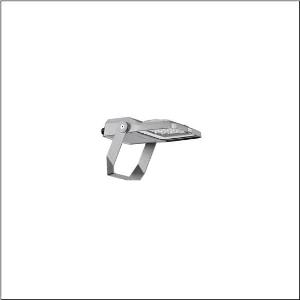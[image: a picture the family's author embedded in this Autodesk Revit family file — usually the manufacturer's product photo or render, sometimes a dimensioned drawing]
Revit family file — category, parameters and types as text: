
# Revit family: floodlight_fl_21_iq_micro___rs12_5xa7762a2b1a_2903
name_source: partatom
category: Lighting Fixtures
units: mm (PartAtom-declared; Revit-internal decimal feet)

## family parameters
Cut with Voids When Loaded = No
Host = Face
Light Source = No
Part Type = Normal
Room Calculation Point = No
Round Connector Dimension = Use Diameter
Shared = No

## types (1)
- --- (1 x LED, 3090 lm, 23.1 W, 3000K)
    Apparent Load = 23 VA
    CIE Flux Codes = 79 92 99 100 100
    Color Rendering = 70
    Color Temperature = 3000K
    Default Elevation = 1800 mm
    Description = Floodlight FL 21 iQ micro, floodlight, primary light control with lens, of PMMA, primary optical cover: protective disc, of toughened safety glass, transparent, light distribution: RS12, light emission: direct distribution, installation type: surface-mounted, LED, High Power LED, rated luminous flux: 3.090lm, luminous efficacy: 134lm/W, light colour: 730, colour temperature: 3000K, control: Auto-Match, Temp-Guard, Night-Set, Smart-Wire, Desk-Remote (wireless, voltage-free reading and setting of iQ features in the workshop via application-optimized NFC function/RFID function), optimised constant luminous flux control (CLO 2.0), Street-Remote, with terminal, 6-pole, mains connection: 220..240V, AC, 50/60Hz, start of lifetime: 23W, end of service life: 24W, reduction: 11W, luminaire housing, of diecast aluminium, powder-coated, Siteco® metallic grey (DB 702S), corrosivity category C5 mid according to DIN EN ISO 12944, sealing non-destructively replaceable, mounting bracket, of steel, galvanised, powder-coated, Siteco® metallic grey (DB 702S), protection rating (complete): IP66, insulation class (complete): insulation class II (safety insulation), certification: CE, ENEC, VDE, protection symbol: D, impact resistance: IK07, permissible operating ambient temperature: -40..+40°C, permissible operating ambient temperature for outdoor applications: -40..+50°C, standard: DIN EN 12944, LABS conformity tested according to VDMA 24364:2018-05, packaging unit: 1 piece

Light Distribution: RS12
    Height = 65 mm
    Lamp = 1 x LED
    Lamp Light Flux = 3090 lm
    Lamp Power = 23.1 W
    Lamp count = 1
    Length = 312 mm
    Luminous efficacy = 134 lm/W
    Manufacturer = Siteco
    ModVariant = No
    Model = 5XA7762A2B1A
    Number of Poles = 1
    OnlyDefault = Yes
    Power Factor = 1
    Product Name = Floodlight FL 21 iQ micro | RS12
    Product group = floodlight | pylon annexe
    ProductGroupID = 6200
    Protection Class = Protection class II
    Protection Degree = IP 66
    RLX_Detail_Level = 1
    RLX_Emergency_Light_Flux = 0 lm
    RLX_Emergency_Type = 0
    RLX_Emergency_Type_DB = No
    RlxData = <blob elided: 75185 chars, md5=a0d5232e>
    Socket = socket
    Standby Power = 0 W
    System Light Flux = 3090 lm
    System Power = 23 W
    Type Comments = factory setting: luminous flux: 100 % | dim-lin: 254 | 455 mA
    Type Image = l_1006880.jpg
    URL = http://relux.com
    VarID = @adj_153367
    Voltage = 0 V
    Weight = 0.00 kg
    Width = 230 mm

## geometry (parser evidence)
native form markers: Blend x4, Sweep x12
no freeform markers — native parametric forms only
